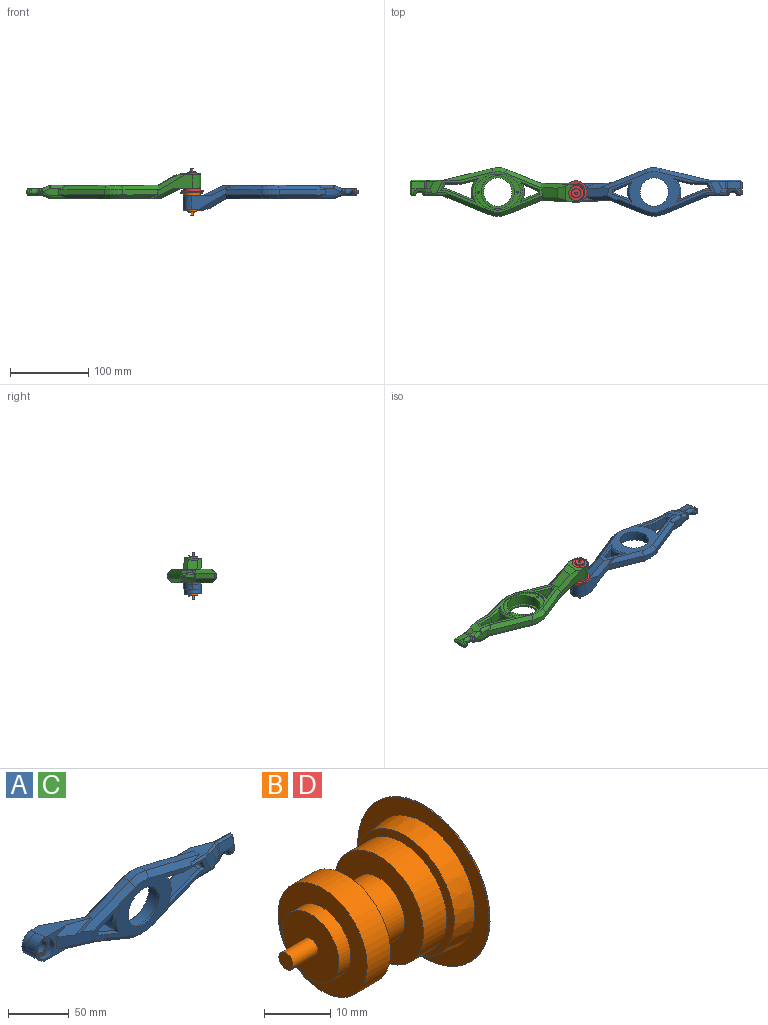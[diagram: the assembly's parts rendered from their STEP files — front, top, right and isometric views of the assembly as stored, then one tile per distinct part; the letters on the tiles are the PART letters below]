
ASSEMBLY  parts=4 mates=3
PART A: 135 faces, bbox 224.9x33.9x63.9 mm
  f0: plane 139.51x53.86mm, normal (0,-1,0), area 2244.2mm2, adj f22,f28,f31,f62,f72,f73,f74,f75
  f1: plane 137.26x53.85mm, normal (0,1,0), area 1171mm2, adj f6,f29,f33,f46,f69,f70,f71,f88
  f2: plane 6.46x2.73mm, normal (0,1,0), area 5.5mm2, adj f45,f55,f63
  f3: plane 10x5mm, normal (0,-1,0), area 21.2mm2, adj f51,f55,f66,f93
  f4: plane 15.67x4mm, normal (1,0,0), area 46.6mm2, adj f90,f91,f92,f93,f94,f95,f96
  f5: plane 25.24x9mm, normal (0,0,-1), area 148.5mm2, adj f8,f16,f46,f47,f48,f49,f59,f60
  f6: plane 61.53x15mm, normal (0,0,1), area 281.4mm2, adj f1,f17,f77,f81,f82,f83,f84,f85
  f7: cylinder r=5mm len=1.61mm, axis (0,-1,0), area 0.4mm2, adj f8,f50,f54,f56,f58
  f8: cylinder r=3mm len=2.78mm, axis (0,-1,0), area 0.4mm2, adj f5,f7,f50,f58
  f9: cylinder r=7.5mm len=15mm, axis (0,-1,0.08), area 11.8mm2, adj f36,f38
  f10: cylinder r=21.08mm len=42.16mm, axis (0,1,0), area 1721.8mm2, adj f32,f34
  f11: cylinder r=11mm len=11.74mm, axis (0,1,0), area 11.5mm2, adj f12,f20,f21,f27
  f12: plane 11.35x10.96mm, normal (0,1,0), area 0.2mm2, adj f11,f21,f27
  f13: plane 46.44x24.4mm, normal (0,0.08,1), area 461.2mm2, adj f19,f20,f21,f23,f27,f30,f80,f99
  f14: plane 45.77x18.72mm, normal (-0.38,0,-0.93), area 337mm2, adj f15,f22,f71,f72,f79
  f15: cylinder r=31mm len=23.41mm, axis (0,1,0), area 168mm2, adj f14,f16,f70,f73
  f16: plane 58.32x23.72mm, normal (0.38,0,-0.93), area 440.7mm2, adj f5,f15,f69,f74
  f17: plane 62.73x15.14mm, normal (0.23,0,0.97), area 451.7mm2, adj f6,f18,f77,f97
  f18: cylinder r=31mm len=19.01mm, axis (0,1,0), area 135.6mm2, adj f17,f19,f76,f98
  f19: plane 60.84x24.88mm, normal (-0.38,0,0.93), area 361.8mm2, adj f13,f18,f28,f30,f75,f99
  f20: plane 36.24x22mm, normal (0,-1,0.08), area 234.4mm2, adj f11,f13,f21,f22,f24,f28,f30,f78
  f21: extruded ~23.33x18.68mm, area 394.9mm2, adj f11,f12,f13,f20,f22,f23
  f22: plane 55.63x30.34mm, normal (0,-0.08,-1), area 508.6mm2, adj f0,f14,f20,f21,f23,f72,f78,f79
  f23: plane 25x22mm, normal (0,1,-0.08), area 201.8mm2, adj f13,f21,f22,f35,f79,f80,f130
  f24: cylinder r=9.54mm len=19.41mm, axis (0,-1,0.08), area 299.6mm2, adj f20,f25
  f25: plane 19.07x19.01mm, normal (0,-1,0.08), area 109mm2, adj f24,f26
  f26: cylinder r=7.5mm len=15mm, axis (0,-1,0.08), area 11.8mm2, adj f25,f39
  f27: cylinder r=11.01mm len=12.51mm, axis (0,1,-0.08), area 182.1mm2, adj f11,f12,f13
  f28: plane 30.03x14.7mm, normal (-0.44,-0.9,0.07), area 335.6mm2, adj f0,f19,f20,f30,f75,f78
  f29: plane 21.45x13.06mm, normal (0.5,0.86,-0.07), area 282mm2, adj f1,f71,f79,f80,f99,f130
  f30: plane 34.44x8.07mm, normal (-0.26,-0.68,0.69), area 191.4mm2, adj f13,f19,f20,f28
  f31: cylinder r=18.08mm len=36.16mm, axis (0,-1,0), area 227.2mm2, adj f0,f32
  f32: plane 42.16x42.16mm, normal (0,1,0), area 369.1mm2, adj f10,f31
  f33: extruded ~58x46mm, area 327.8mm2, adj f1,f34
  f34: plane 58x46mm, normal (0,1,0), area 688.8mm2, adj f10,f33,f131,f133
  f35: cylinder r=9.54mm len=19.41mm, axis (0,-1,0.08), area 299.6mm2, adj f23,f36
  f36: plane 19.07x19.01mm, normal (0,1,-0.08), area 109mm2, adj f9,f35
  f37: cylinder r=5.75mm len=11.97mm, axis (0,-1,0.08), area 234.8mm2, adj f38,f39
  f38: plane 15x14.95mm, normal (0,1,-0.08), area 72.8mm2, adj f9,f37
  f39: plane 15x14.95mm, normal (0,-1,0.08), area 72.8mm2, adj f26,f37
  f40: plane 7.55x5mm, normal (0.37,-0.93,0), area 34.6mm2, adj f44,f60,f68,f89
  f41: plane 6.46x2.73mm, normal (0,-1,0), area 5.5mm2, adj f44,f55,f66
  f42: plane 7.55x5mm, normal (0.37,0.93,0), area 34.6mm2, adj f45,f48,f65,f88
  f43: plane 10x5mm, normal (0,1,0), area 21.2mm2, adj f51,f55,f63,f96
  f44: cylinder r=5mm len=5mm, axis (0,0,1), area 8.5mm2, adj f40,f41,f56,f59,f67
  f45: cylinder r=5mm len=5mm, axis (0,0,1), area 8.5mm2, adj f2,f42,f49,f54,f64
  f46: cylinder r=4mm len=17.63mm, axis (1,0,0), area 100mm2, adj f1,f5,f47,f69,f88
  f47: torus R=1mm, axis (0,0,-1), area 5.5mm2, adj f5,f46,f48,f88
  f48: cylinder r=4mm len=10.99mm, axis (0.93,-0.37,0), area 62.8mm2, adj f5,f42,f47,f49,f88
  f49: torus R=9mm, axis (0,0,-1), area 9.9mm2, adj f5,f45,f48,f50,f52
  f50: bspline ~2.8x1.9mm, area 1.4mm2, adj f7,f8,f49,f52
  f51: cylinder r=4mm len=8mm, axis (1,0,0), area 28.4mm2, adj f3,f43,f53,f95
  f52: bspline ~4.65x4mm, area 8.3mm2, adj f49,f50,f54
  f53: bspline ~8x4mm, area 19.4mm2, adj f51,f55
  f54: bspline ~6.25x4.85mm, area 11.7mm2, adj f7,f45,f52,f55
  f55: torus R=9mm, axis (0,1,0), area 157.7mm2, adj f2,f3,f41,f43,f53,f54,f56
  f56: bspline ~6.25x4.85mm, area 11.7mm2, adj f7,f44,f55,f57
  f57: bspline ~4.65x4mm, area 8.3mm2, adj f56,f58,f59
  f58: bspline ~2.84x1.9mm, area 1.4mm2, adj f7,f8,f57,f59
  f59: torus R=9mm, axis (0,0,-1), area 9.9mm2, adj f5,f44,f57,f58,f60
  f60: cylinder r=4mm len=10.99mm, axis (-0.93,-0.37,0), area 62.8mm2, adj f5,f40,f59,f61,f89
  f61: torus R=1mm, axis (0,0,-1), area 5.5mm2, adj f5,f60,f62,f89
  f62: cylinder r=4mm len=17.63mm, axis (-1,0,0), area 100mm2, adj f0,f5,f61,f74,f89
  f63: plane 16.46x9.36mm, normal (0,0.98,0.18), area 156.5mm2, adj f2,f43,f64,f83,f94
  f64: cone r=7mm half-angle=10.3deg, axis (0,0,1), area 21.1mm2, adj f45,f63,f65,f82
  f65: plane 9.91x9.36mm, normal (0.36,0.91,0.18), area 74.7mm2, adj f42,f64,f81,f88
  f66: plane 16.46x9.36mm, normal (0,-0.98,0.18), area 156.5mm2, adj f3,f41,f67,f87,f91
  f67: cone r=7mm half-angle=10.3deg, axis (0,0,1), area 21.1mm2, adj f44,f66,f68,f86
  f68: plane 9.91x9.36mm, normal (0.36,-0.91,0.18), area 74.7mm2, adj f40,f67,f85,f89
  f69: plane 60.21x27.72mm, normal (0.27,0.71,-0.66), area 414.6mm2, adj f1,f5,f16,f46,f70
  f70: cone r=31mm half-angle=45deg, axis (0,-1,0), area 156.1mm2, adj f1,f15,f69,f71
  f71: plane 47.67x24.01mm, normal (-0.27,0.71,-0.65), area 350.6mm2, adj f1,f14,f29,f70,f79
  f72: plane 46.77x18.75mm, normal (-0.27,-0.71,-0.65), area 303.3mm2, adj f0,f14,f22,f73
  f73: cone r=26mm half-angle=45deg, axis (0,1,0), area 156.1mm2, adj f0,f15,f72,f74
  f74: plane 60.21x27.72mm, normal (0.27,-0.71,-0.66), area 414.6mm2, adj f0,f5,f16,f62,f73
  f75: plane 58.2x24.31mm, normal (-0.27,-0.71,0.65), area 398.9mm2, adj f0,f19,f28,f76
  f76: cone r=26mm half-angle=45deg, axis (0,1,0), area 125.9mm2, adj f0,f18,f75,f77
  f77: plane 63.9x17.14mm, normal (0.17,-0.71,0.69), area 395.1mm2, adj f0,f6,f17,f76,f84
  f78: plane 39.17x13.79mm, normal (-0.31,-0.69,-0.66), area 220.9mm2, adj f0,f20,f22,f28
  f79: plane 35.22x20.72mm, normal (0.36,0.55,-0.75), area 230.8mm2, adj f14,f22,f23,f29,f71,f130
  f80: plane 35.67x20.57mm, normal (0.36,0.66,0.66), area 241.1mm2, adj f13,f23,f29,f99,f130
  f81: plane 18.71x7.17mm, normal (0.24,0.6,0.77), area 37.6mm2, adj f6,f65,f82,f88
  f82: cone r=8.67mm half-angle=50.2deg, axis (0,0,1), area 7.5mm2, adj f6,f64,f81,f83
  f83: plane 16.46x1.97mm, normal (0,0.64,0.77), area 42.2mm2, adj f6,f63,f82,f92
  f84: plane 20.01x2mm, normal (0,-0.71,0.71), area 51.1mm2, adj f0,f6,f77,f85,f89
  f85: plane 14.66x6.36mm, normal (0.24,-0.6,0.77), area 34.9mm2, adj f6,f68,f84,f86,f89
  f86: cone r=8.67mm half-angle=50.2deg, axis (0,0,1), area 7.5mm2, adj f6,f67,f85,f87
  f87: plane 16.46x1.97mm, normal (0,-0.64,0.77), area 42.2mm2, adj f6,f66,f86,f90
  f88: plane 18.32x16.77mm, normal (0.19,0.98,0.09), area 161.8mm2, adj f1,f6,f42,f46,f47,f48,f65,f81
  f89: plane 17.52x15.78mm, normal (0.19,-0.98,0.09), area 154.5mm2, adj f0,f40,f60,f61,f62,f68,f84,f85
  f90: plane 2.71x2.3mm, normal (0.71,-0.45,0.54), area 5mm2, adj f4,f6,f87,f91,f92
  f91: plane 9.54x3.54mm, normal (0.71,-0.7,0.13), area 25.6mm2, adj f4,f66,f90,f93
  f92: plane 2.71x2.3mm, normal (0.71,0.45,0.54), area 5mm2, adj f4,f6,f83,f90,f94
  f93: plane 5x2mm, normal (0.71,-0.71,0), area 13.9mm2, adj f3,f4,f91,f95
  f94: plane 9.54x3.54mm, normal (0.71,0.7,0.13), area 25.6mm2, adj f4,f63,f92,f96
  f95: cone r=2mm half-angle=45deg, axis (-1,0,0), area 26.7mm2, adj f4,f51,f93,f96
  f96: plane 5x2mm, normal (0.71,0.71,0), area 13.9mm2, adj f4,f43,f94,f95
  f97: plane 63.9x15.14mm, normal (0.17,0.71,0.69), area 383mm2, adj f1,f6,f17,f98
  f98: cone r=31mm half-angle=45deg, axis (0,-1,0), area 125.9mm2, adj f1,f18,f97,f99
  f99: plane 46.05x23.46mm, normal (-0.27,0.71,0.65), area 341.4mm2, adj f1,f13,f19,f29,f80,f98
  f100: extruded ~23.52x13mm, area 322.1mm2, adj f101,f105,f116,f125
  f101: plane 18.74x13mm, normal (-0.23,0,-0.97), area 250.5mm2, adj f100,f102,f114,f124
  f102: plane 18.97x13mm, normal (0,0,-1), area 246.5mm2, adj f101,f103,f115,f126
  f103: plane 13x5.4mm, normal (-0.9,0,-0.44), area 78.2mm2, adj f102,f104,f117,f128
  f104: plane 13x4.14mm, normal (0,0,1), area 53.9mm2, adj f103,f105,f119,f129
  f105: plane 33.44x13.6mm, normal (-0.38,0,0.93), area 469.3mm2, adj f100,f104,f118,f127
  f106: plane 13x2.82mm, normal (0.99,0,-0.13), area 37mm2, adj f107,f109,f113,f123
  f107: plane 18.94x13mm, normal (0.38,0,-0.93), area 265.9mm2, adj f106,f108,f112,f121
  f108: extruded ~18.46x13mm, area 246.6mm2, adj f107,f109,f110,f120
  f109: plane 19.31x13mm, normal (0.38,0,0.93), area 271.3mm2, adj f106,f108,f111,f122
  f110: bspline ~27.38x5.61mm, area 65.1mm2, adj f1,f108,f111,f112
  f111: plane 25.23x11.59mm, normal (0.27,0.71,0.65), area 68mm2, adj f1,f109,f110,f113
  f112: plane 24.5x11.44mm, normal (0.27,0.71,-0.65), area 66.3mm2, adj f1,f107,f110,f113
  f113: plane 5.5x2.57mm, normal (0.7,0.71,-0.09), area 11.9mm2, adj f1,f106,f111,f112
  f114: plane 23.72x7.73mm, normal (-0.17,0.71,-0.69), area 61.7mm2, adj f1,f101,f115,f116
  f115: plane 20.21x2mm, normal (0,0.71,-0.71), area 55.1mm2, adj f1,f102,f114,f117
  f116: bspline ~32.34x9.42mm, area 81.6mm2, adj f1,f100,f114,f118
  f117: plane 9.4x5.86mm, normal (-0.63,0.71,-0.31), area 23.3mm2, adj f1,f103,f115,f119
  f118: plane 37.58x17.29mm, normal (-0.27,0.71,0.66), area 108.4mm2, adj f1,f105,f116,f119
  f119: plane 7.35x2mm, normal (0,0.71,0.71), area 15.7mm2, adj f1,f104,f117,f118
  f120: bspline ~27.38x5.61mm, area 65.1mm2, adj f0,f108,f121,f122
  f121: plane 24.5x11.44mm, normal (0.27,-0.71,-0.65), area 66.3mm2, adj f0,f107,f120,f123
  f122: plane 25.23x11.59mm, normal (0.27,-0.71,0.65), area 68mm2, adj f0,f109,f120,f123
  f123: plane 5.5x2.57mm, normal (0.7,-0.71,-0.09), area 11.9mm2, adj f0,f106,f121,f122
  f124: plane 23.72x7.73mm, normal (-0.17,-0.71,-0.69), area 61.7mm2, adj f0,f101,f125,f126
  f125: bspline ~32.34x9.42mm, area 81.6mm2, adj f0,f100,f124,f127
  f126: plane 20.21x2mm, normal (0,-0.71,-0.71), area 55.1mm2, adj f0,f102,f124,f128
  f127: plane 37.58x17.29mm, normal (-0.27,-0.71,0.66), area 108.4mm2, adj f0,f105,f125,f129
  f128: plane 9.4x5.86mm, normal (-0.63,-0.71,-0.31), area 23.3mm2, adj f0,f103,f126,f129
  f129: plane 7.35x2mm, normal (0,-0.71,0.71), area 15.7mm2, adj f0,f104,f127,f128
  f130: plane 17.06x9.32mm, normal (0.26,0.96,-0.08), area 140.8mm2, adj f23,f29,f79,f80
  f131: cylinder r=1.3mm len=13mm, axis (0,1,0), area 106.2mm2, adj f34,f132
  f132: plane 2.6x2.6mm, normal (0,1,0), area 5.3mm2, adj f131
  f133: cylinder r=1.3mm len=13mm, axis (0,1,0), area 106.2mm2, adj f34,f134
  f134: plane 2.6x2.6mm, normal (0,1,0), area 5.3mm2, adj f133
PART B: 19 faces, bbox 30x28x28 mm
  f0: plane 12x12mm, normal (-1,0,0), area 106mm2, adj f1,f18
  f1: cylinder r=1.5mm len=5.3mm, axis (-1,0,0), area 50mm2, adj f0,f2
  f2: plane 3x3mm, normal (-1,0,0), area 7.1mm2, adj f1
  f3: plane 6x6mm, normal (1,0,0), area 28.3mm2, adj f4
  f4: cone r=2.5mm half-angle=45deg, axis (1,0,0), area 12.2mm2, adj f3,f5
  f5: plane 28x28mm, normal (1,0,0), area 596.1mm2, adj f4,f6
  f6: cylinder r=14mm len=28mm, axis (-1,0,0), area 17.6mm2, adj f5,f7
  f7: plane 28x28mm, normal (-1,0,0), area 235.6mm2, adj f6,f8
  f8: cone r=10.58mm half-angle=6deg, axis (1,0,0), area 272.7mm2, adj f7,f9
  f9: plane 21.16x21.16mm, normal (-1,0,0), area 238.5mm2, adj f8,f10
  f10: cylinder r=6mm len=12mm, axis (-1,0,0), area 18.8mm2, adj f9,f11
  f11: plane 19x19mm, normal (1,0,0), area 170.4mm2, adj f10,f12
  f12: cylinder r=9.5mm len=19mm, axis (-1,0,0), area 298.5mm2, adj f11,f13
  f13: plane 19x19mm, normal (-1,0,0), area 188.5mm2, adj f12,f14
  f14: cylinder r=5.5mm len=11mm, axis (-1,0,0), area 241.9mm2, adj f13,f15
  f15: plane 19x19mm, normal (1,0,0), area 188.5mm2, adj f14,f16
  f16: cylinder r=9.5mm len=19mm, axis (-1,0,0), area 298.5mm2, adj f15,f17
  f17: plane 19x19mm, normal (-1,0,0), area 170.4mm2, adj f16,f18
  f18: cylinder r=6mm len=12mm, axis (-1,0,0), area 94.2mm2, adj f0,f17
PART C: same geometry as A
PART D: same geometry as B
PLACE A rot(axis=(-1,0,0),90deg) t=(179.03,-27.61,185.39)mm
PLACE B rot(axis=(0.71,0.03,0.71),176.8deg) t=(79.03,-27.2,193.32)mm
PLACE C rot(axis=(0,-0.71,-0.71),180deg) t=(-20.67,-27.69,202.39)mm
PLACE D rot(axis=(-0.71,-0.03,0.71),176.8deg) t=(79.33,-27.28,194.47)mm
MATE fastened B.f1 <-> A.f24  axis (0,-0.08,-1) through (79.03,-28,183.15)mm
MATE planar C.f0 <-> A.f1  axis (0,0,-1) through (-23.18,-27.1,185.39)mm
MATE fastened D.f1 <-> C.f24  axis (0,-0.08,1) through (79.33,-28.08,204.64)mm
